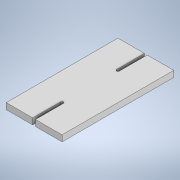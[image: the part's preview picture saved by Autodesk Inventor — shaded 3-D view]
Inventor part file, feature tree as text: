
AUTODESK INVENTOR PART (.ipt)
format: ipt  version: 2020 (Build 240168000, 168)  size: 103,936 bytes
history: native  units: mm
features: extrude x1, sketch x1
ambient origin geometry x8: Origin, YZ Plane, XZ Plane, XY Plane, X Axis, Y Axis, Z Axis, Center Point
bodies: Solide1 (feature_tree)
feature tree (2):
  extrude  "Extrusion1"  Depth=200.0mm
  sketch  "Esquisse1"
